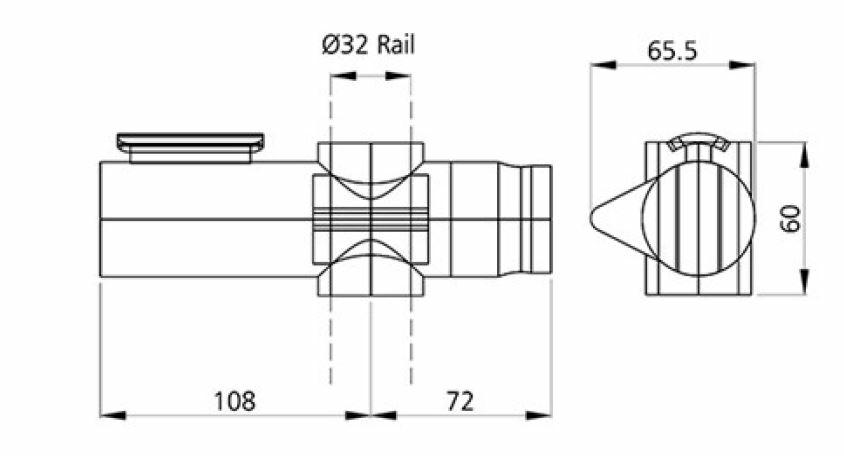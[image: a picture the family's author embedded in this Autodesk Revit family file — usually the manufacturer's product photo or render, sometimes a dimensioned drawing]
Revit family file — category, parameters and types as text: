
# Revit family: rba-bim-rba4110-999 Series
name_source: partatom
category: Plumbing Fixtures
revit_build: Autodesk Revit 2016 (Build: 20151007_0715(x64)
units: mm (PartAtom-declared; Revit-internal decimal feet)

## family parameters
Always vertical = Yes
Cut with Voids When Loaded = No
Part Type = Normal
Room Calculation Point = No
Round Connector Dimension = Use Diameter
Shared = Yes
Work Plane-Based = No

## types (3) — shared parameters
CW Connection = Yes
Description = ënda Shower Rail Handset Slider
HW Connection = Yes
Manufacturer = RBA Group
Modified Issue = 20191114.01
Vent Connection = Yes
Waste Connection = Yes

## per-type parameters (varying)
| type | Materials and Finishes |
| RBA4110-999-011 | Chrome Plated ABS |
| RBA4110-999-013 | Satin Plated ABS |
| RBA4110-999-014 | Matte Black ABS |

note: column(s) folded — value = type name in every type: Model

## geometry (parser evidence)
native form markers: Blend x2, Sweep x2
no freeform markers — native parametric forms only
